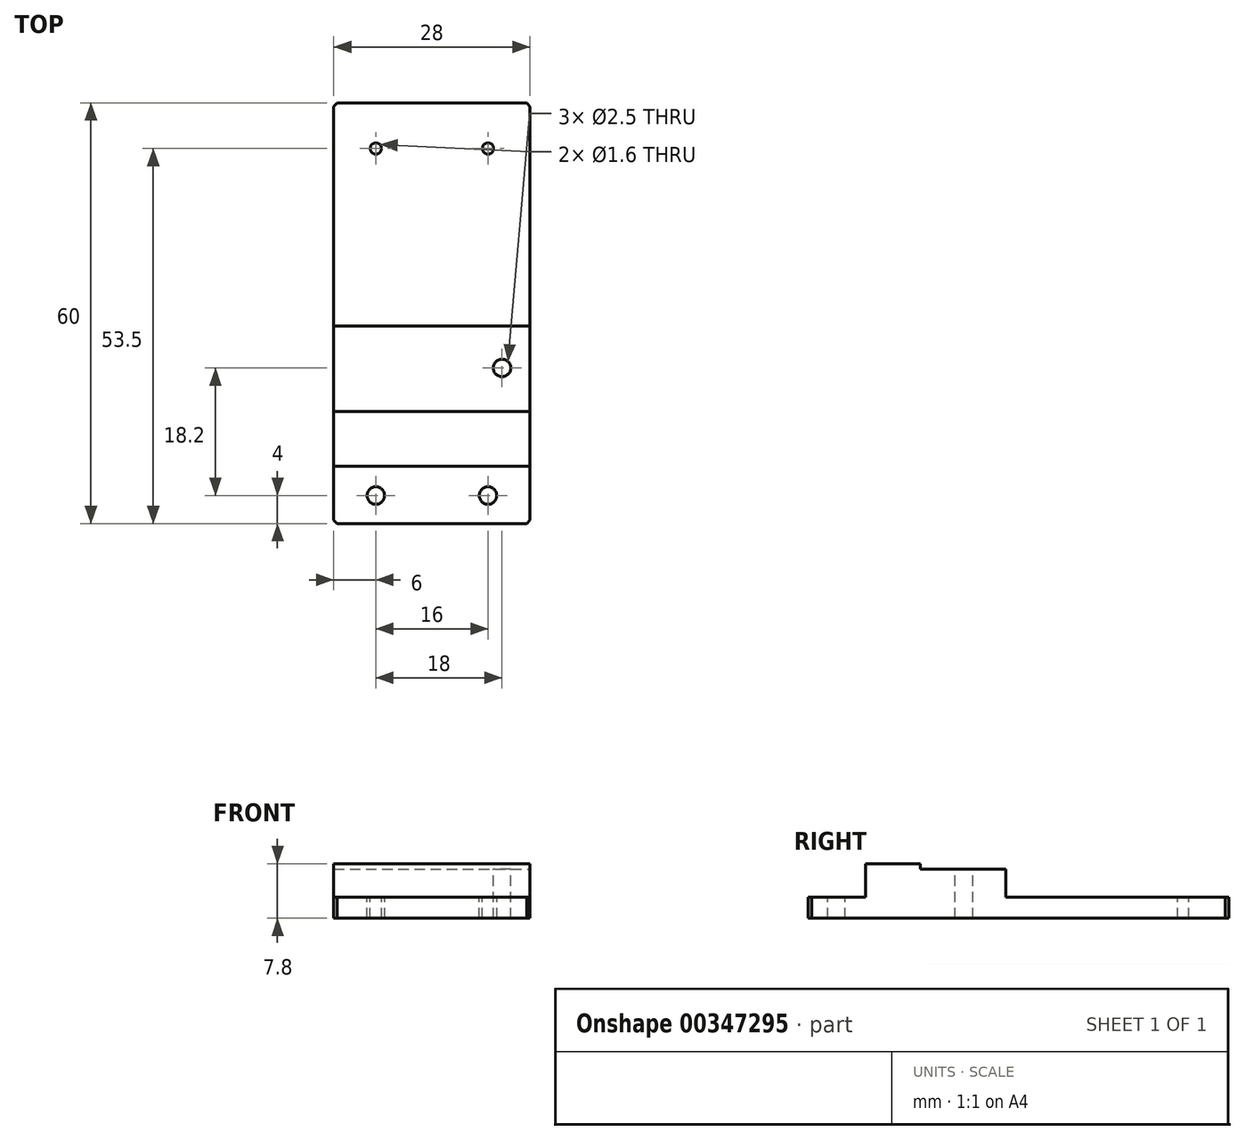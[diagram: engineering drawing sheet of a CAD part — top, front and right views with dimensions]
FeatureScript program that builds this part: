
annotation { "Feature Type Name" : "Feature", "Feature Type Description" : "" }
export const myFeature = defineFeature(function(context is Context, id is Id, definition is map)
    precondition{}
    {
        {
            var Q0;
            Q0=qCreatedBy(makeId("Top.planeOp"),FACE);
            var sketch = newSketch(context, id + "F0", { "sketchPlane" : qUnion([Q0])});
            skLineSegment(sketch, "E0.bottom", {"start": v(0, 0) * mm, "end": v(28, 0) * mm});
            skLineSegment(sketch, "E0.top", {"start": v(0, 60) * mm, "end": v(28, 60) * mm});
            skLineSegment(sketch, "E0.left", {"start": v(0, 0) * mm, "end": v(0, 60) * mm});
            skLineSegment(sketch, "E0.right", {"start": v(28, 0) * mm, "end": v(28, 60) * mm});
            skSolve(sketch);
        }
        {
            var Q0;
            Q0=makeQuery(id+"F0.imprint","IMPRINT",FACE,{"disambiguationData":[TD([[makeQuery(id+"F0.imprint","IMPRINT",EDGE,{"derivedFrom":sQuery(id+"F0.wireOp",EDGE,"E0.bottom")}),1.0]])]});
            var sketch = newSketch(context, id + "F1", { "sketchPlane" : qUnion([Q0])});
            skLineSegment(sketch, "E1.bottom", {"start": v(0, 0) * mm, "end": v(28, 0) * mm});
            skLineSegment(sketch, "E1.top", {"start": v(0, 8.2) * mm, "end": v(28, 8.2) * mm});
            skLineSegment(sketch, "E1.left", {"start": v(0, 0) * mm, "end": v(0, 8.2) * mm});
            skLineSegment(sketch, "E1.right", {"start": v(28, 0) * mm, "end": v(28, 8.2) * mm});
            skSolve(sketch);
        }
        {
            var Q0;
            Q0=makeQuery(id+"F0.imprint","IMPRINT",FACE,{"disambiguationData":[TD([[makeQuery(id+"F0.imprint","IMPRINT",EDGE,{"derivedFrom":sQuery(id+"F0.wireOp",EDGE,"E0.bottom")}),1.0]])]});
            var sketch = newSketch(context, id + "F2", { "sketchPlane" : qUnion([Q0])});
            skLineSegment(sketch, "E2.bottom", {"start": v(0, 8.2) * mm, "end": v(28, 8.2) * mm});
            skLineSegment(sketch, "E2.top", {"start": v(0, 16) * mm, "end": v(28, 16) * mm});
            skLineSegment(sketch, "E2.left", {"start": v(0, 8.2) * mm, "end": v(0, 16) * mm});
            skLineSegment(sketch, "E2.right", {"start": v(28, 8.2) * mm, "end": v(28, 16) * mm});
            skSolve(sketch);
        }
        {
            var Q0;
            Q0=makeQuery(id+"F0.imprint","IMPRINT",FACE,{"disambiguationData":[TD([[makeQuery(id+"F0.imprint","IMPRINT",EDGE,{"derivedFrom":sQuery(id+"F0.wireOp",EDGE,"E0.bottom")}),1.0]])]});
            var sketch = newSketch(context, id + "F3", { "sketchPlane" : qUnion([Q0])});
            skLineSegment(sketch, "E3.bottom", {"start": v(0, 16) * mm, "end": v(28, 16) * mm});
            skLineSegment(sketch, "E3.top", {"start": v(0, 28.2) * mm, "end": v(28, 28.2) * mm});
            skLineSegment(sketch, "E3.left", {"start": v(0, 16) * mm, "end": v(0, 28.2) * mm});
            skLineSegment(sketch, "E3.right", {"start": v(28, 16) * mm, "end": v(28, 28.2) * mm});
            skSolve(sketch);
        }
        {
            var Q0;
            Q0 = qSketchRegion(id + "F0", true);
            extrude(context, id + "F4", {"entities" : qUnion([Q0]), "depth" : 3 * mm});
        }
        {
            var Q0;
            Q0 = qSketchRegion(id + "F2", true);
            extrude(context, id + "F5", {"entities" : qUnion([Q0]), "operationType" : NewBodyOperationType.ADD, "depth" : 7.8 * mm});
        }
        {
            var Q0;
            Q0 = qSketchRegion(id + "F3", true);
            extrude(context, id + "F6", {"entities" : qUnion([Q0]), "operationType" : NewBodyOperationType.ADD, "depth" : 7 * mm});
        }
        {
            var Q0;
            {var subQ0=sQuery(id+"F0.wireOp",EDGE,"E0.right");var subQ1=sQuery(id+"F0.wireOp",EDGE,"E0.left");var subQ2=sQuery(id+"F0.wireOp",EDGE,"E0.top");Q0=makeQuery(id+"F5.boolean.opBoolean","SPLIT",FACE,{"disambiguationData":[TD([makeQuery(id+"F4.opExtrude","SWEPT_FACE",FACE,{"disambiguationData":[OSD([subQ2])]})])],"derivedFrom":makeQuery(id+"F4.opExtrude","CAP_FACE",FACE,{"disambiguationData":[OSD([sQuery(id+"F0.wireOp",EDGE,"E0.bottom"),subQ2,subQ1,subQ0])],"isStart":false})});}
            var sketch = newSketch(context, id + "F7", { "sketchPlane" : qUnion([Q0])});
            skCircle(sketch, "E4", {"center": v(6, 53.5) * mm, "radius": 0.8 * mm});
            skSolve(sketch);
        }
        {
            var Q0;
            Q0=makeQuery(id+"F7.imprint","IMPRINT",FACE,{"disambiguationData":[TD([[makeQuery(id+"F7.imprint","IMPRINT",EDGE,{"derivedFrom":sQuery(id+"F7.wireOp",EDGE,"E4")}),1.0]])]});
            extrude(context, id + "F8", {"entities" : qUnion([Q0]), "operationType" : NewBodyOperationType.REMOVE, "oppositeDirection" : true, "depth" : 25 * mm});
        }
        {
            var Q0;
            {var subQ0=sQuery(id+"F0.wireOp",EDGE,"E0.right");var subQ1=sQuery(id+"F0.wireOp",EDGE,"E0.left");var subQ2=sQuery(id+"F0.wireOp",EDGE,"E0.top");Q0=makeQuery(id+"F5.boolean.opBoolean","SPLIT",FACE,{"disambiguationData":[TD([makeQuery(id+"F4.opExtrude","SWEPT_FACE",FACE,{"disambiguationData":[OSD([subQ2])]})])],"derivedFrom":makeQuery(id+"F4.opExtrude","CAP_FACE",FACE,{"disambiguationData":[OSD([sQuery(id+"F0.wireOp",EDGE,"E0.bottom"),subQ2,subQ1,subQ0])],"isStart":false})});}
            var sketch = newSketch(context, id + "F9", { "sketchPlane" : qUnion([Q0])});
            skCircle(sketch, "E5", {"center": v(22, 53.5) * mm, "radius": 0.8 * mm});
            skSolve(sketch);
        }
        {
            var Q0;
            Q0=makeQuery(id+"F9.imprint","IMPRINT",FACE,{"disambiguationData":[TD([[makeQuery(id+"F9.imprint","IMPRINT",EDGE,{"derivedFrom":sQuery(id+"F9.wireOp",EDGE,"E5")}),1.0]])]});
            extrude(context, id + "F10", {"entities" : qUnion([Q0]), "operationType" : NewBodyOperationType.REMOVE, "oppositeDirection" : true, "depth" : 25 * mm});
        }
        {
            var Q0;
            {var subQ0=sQuery(id+"F0.wireOp",EDGE,"E0.left");var subQ1=sQuery(id+"F0.wireOp",EDGE,"E0.right");var subQ2=sQuery(id+"F0.wireOp",EDGE,"E0.bottom");Q0=makeQuery(id+"F5.boolean.opBoolean","SPLIT",FACE,{"disambiguationData":[TD([makeQuery(id+"F4.opExtrude","SWEPT_FACE",FACE,{"disambiguationData":[OSD([subQ2])]})])],"derivedFrom":makeQuery(id+"F4.opExtrude","CAP_FACE",FACE,{"disambiguationData":[OSD([subQ2,sQuery(id+"F0.wireOp",EDGE,"E0.top"),subQ0,subQ1])],"isStart":false})});}
            var sketch = newSketch(context, id + "F11", { "sketchPlane" : qUnion([Q0])});
            skCircle(sketch, "E6", {"center": v(6, 4) * mm, "radius": 1.25 * mm});
            skSolve(sketch);
        }
        {
            var Q0;
            Q0=makeQuery(id+"F11.imprint","IMPRINT",FACE,{"disambiguationData":[TD([[makeQuery(id+"F11.imprint","IMPRINT",EDGE,{"derivedFrom":sQuery(id+"F11.wireOp",EDGE,"E6")}),-1.0]])]});
            var sketch = newSketch(context, id + "F12", { "sketchPlane" : qUnion([Q0])});
            skCircle(sketch, "E7", {"center": v(22, 4) * mm, "radius": 1.25 * mm});
            skSolve(sketch);
        }
        {
            var Q0;
            Q0=makeQuery(id+"F11.imprint","IMPRINT",FACE,{"disambiguationData":[TD([[makeQuery(id+"F11.imprint","IMPRINT",EDGE,{"derivedFrom":sQuery(id+"F11.wireOp",EDGE,"E6")}),1.0]])]});
            extrude(context, id + "F13", {"entities" : qUnion([Q0]), "operationType" : NewBodyOperationType.REMOVE, "oppositeDirection" : true, "depth" : 25 * mm});
        }
        {
            var Q0;
            Q0=makeQuery(id+"F12.imprint","IMPRINT",FACE,{"disambiguationData":[TD([[makeQuery(id+"F12.imprint","IMPRINT",EDGE,{"derivedFrom":sQuery(id+"F12.wireOp",EDGE,"E7")}),1.0]])]});
            extrude(context, id + "F14", {"entities" : qUnion([Q0]), "operationType" : NewBodyOperationType.REMOVE, "oppositeDirection" : true, "depth" : 25 * mm});
        }
        {
            var Q0;
            Q0=makeQuery(id+"F4.opExtrude","SWEPT_EDGE",EDGE,{"disambiguationData":[OSD([sQuery(id+"F0.wireOp",EDGE,"E0.bottom"),sQuery(id+"F0.wireOp",EDGE,"E0.right")])]});
            var Q1;
            Q1=makeQuery(id+"F4.opExtrude","SWEPT_EDGE",EDGE,{"disambiguationData":[OSD([sQuery(id+"F0.wireOp",EDGE,"E0.bottom"),sQuery(id+"F0.wireOp",EDGE,"E0.left")])]});
            var Q2;
            Q2=makeQuery(id+"F4.opExtrude","SWEPT_EDGE",EDGE,{"disambiguationData":[OSD([sQuery(id+"F0.wireOp",EDGE,"E0.top"),sQuery(id+"F0.wireOp",EDGE,"E0.left")])]});
            var Q3;
            Q3=makeQuery(id+"F4.opExtrude","SWEPT_EDGE",EDGE,{"disambiguationData":[OSD([sQuery(id+"F0.wireOp",EDGE,"E0.top"),sQuery(id+"F0.wireOp",EDGE,"E0.right")])]});
            chamfer(context, id + "F15", {"entities" : qUnion([Q0, Q1, Q2, Q3]), "width" : 0.5 * mm, "tangentPropagation" : true});
        }
        {
            var Q0;
            Q0=makeQuery(id+"F6.opExtrude","CAP_FACE",FACE,{"disambiguationData":[OSD([sQuery(id+"F3.wireOp",EDGE,"E3.bottom"),sQuery(id+"F3.wireOp",EDGE,"E3.top"),sQuery(id+"F3.wireOp",EDGE,"E3.left"),sQuery(id+"F3.wireOp",EDGE,"E3.right")])],"isStart":false});
            var sketch = newSketch(context, id + "F16", { "sketchPlane" : qUnion([Q0])});
            skCircle(sketch, "E8", {"center": v(24, 22.2) * mm, "radius": 1.25 * mm});
            skSolve(sketch);
        }
        {
            var Q0;
            Q0=makeQuery(id+"F16.imprint","IMPRINT",FACE,{"disambiguationData":[TD([[makeQuery(id+"F16.imprint","IMPRINT",EDGE,{"derivedFrom":sQuery(id+"F16.wireOp",EDGE,"E8")}),1.0]])]});
            var Q1;
            Q1=sQuery(id+"F16.wireOp",EDGE,"E8");
            extrude(context, id + "F17", {"entities" : qUnion([Q0]), "operationType" : NewBodyOperationType.REMOVE, "surfaceEntities" : qUnion([Q1]), "oppositeDirection" : true, "depth" : 25 * mm});
        }
    });
